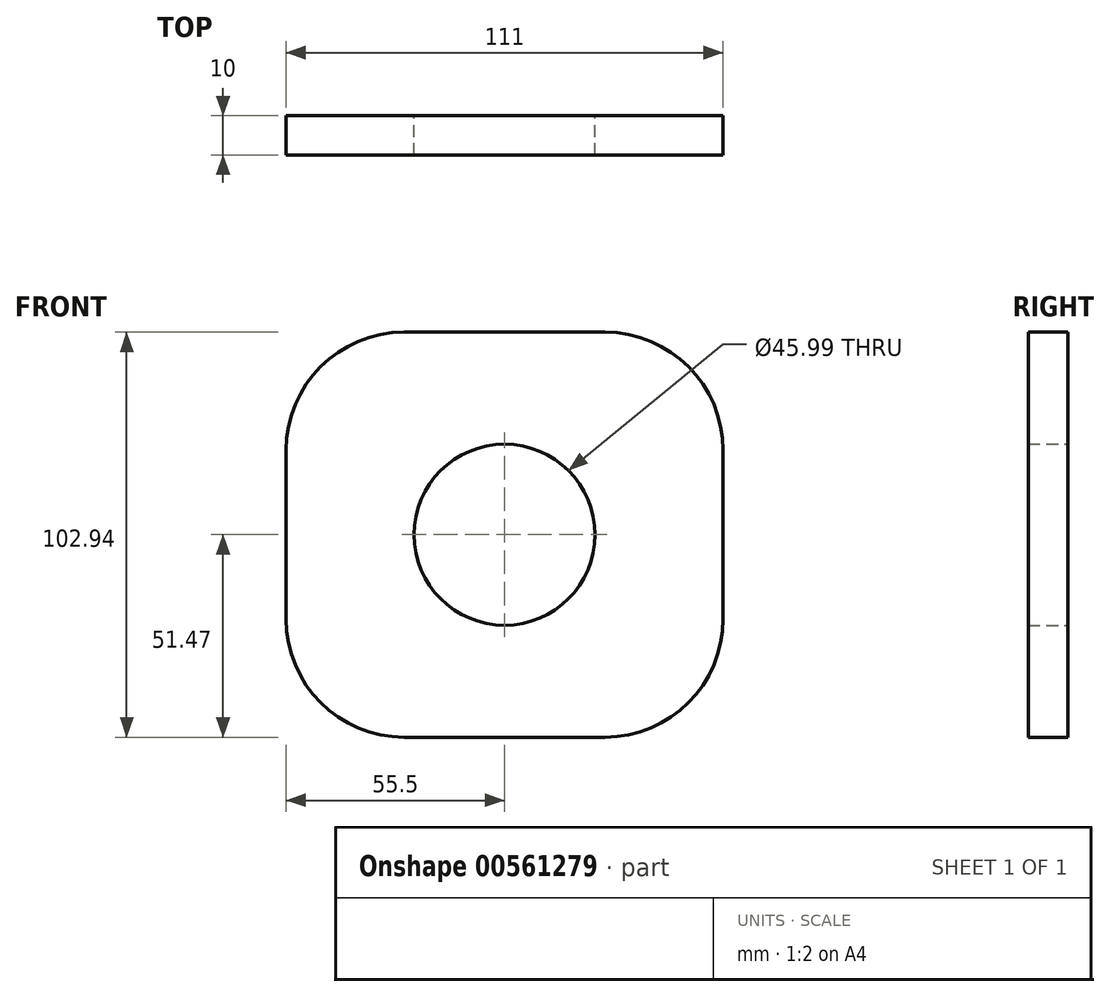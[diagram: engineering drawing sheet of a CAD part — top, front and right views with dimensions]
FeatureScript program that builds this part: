
annotation { "Feature Type Name" : "Feature", "Feature Type Description" : "" }
export const myFeature = defineFeature(function(context is Context, id is Id, definition is map)
    precondition{}
    {
        {
            var Q0;
            Q0=qCreatedBy(makeId("Front.planeOp"),FACE);
            var sketch = newSketch(context, id + "F0", { "sketchPlane" : qUnion([Q0])});
            skLineSegment(sketch, "E0.bottom", {"start": v(55.5, 51.47) * mm, "end": v(-55.5, 51.47) * mm});
            skLineSegment(sketch, "E0.top", {"start": v(55.5, -51.47) * mm, "end": v(-55.5, -51.47) * mm});
            skLineSegment(sketch, "E0.left", {"start": v(55.5, 51.47) * mm, "end": v(55.5, -51.47) * mm});
            skLineSegment(sketch, "E0.right", {"start": v(-55.5, 51.47) * mm, "end": v(-55.5, -51.47) * mm});
            skPoint(sketch, "E0.middle", {"position": v(0, 0) * mm});
            skCircle(sketch, "E1", {"center": v(0, 0) * mm, "radius": 23 * mm});
            skSolve(sketch);
        }
        {
            var Q0;
            Q0=makeQuery(id+"F0.imprint","IMPRINT",FACE,{"disambiguationData":[TD([[makeQuery(id+"F0.imprint","IMPRINT",EDGE,{"derivedFrom":sQuery(id+"F0.wireOp",EDGE,"E0.bottom")}),1.0]])]});
            extrude(context, id + "F1", {"entities" : qUnion([Q0]), "depth" : 10 * mm, "offsetDistance" : 25 * mm});
        }
        {
            var Q0;
            Q0=makeQuery(id+"F1.opExtrude","SWEPT_EDGE",EDGE,{"disambiguationData":[OSD([sQuery(id+"F0.wireOp",EDGE,"E0.bottom"),sQuery(id+"F0.wireOp",EDGE,"E0.right")])]});
            var Q1;
            Q1=makeQuery(id+"F1.opExtrude","SWEPT_EDGE",EDGE,{"disambiguationData":[OSD([sQuery(id+"F0.wireOp",EDGE,"E0.top"),sQuery(id+"F0.wireOp",EDGE,"E0.right")])]});
            var Q2;
            Q2=makeQuery(id+"F1.opExtrude","SWEPT_EDGE",EDGE,{"disambiguationData":[OSD([sQuery(id+"F0.wireOp",EDGE,"E0.top"),sQuery(id+"F0.wireOp",EDGE,"E0.left")])]});
            var Q3;
            Q3=makeQuery(id+"F1.opExtrude","SWEPT_EDGE",EDGE,{"disambiguationData":[OSD([sQuery(id+"F0.wireOp",EDGE,"E0.bottom"),sQuery(id+"F0.wireOp",EDGE,"E0.left")])]});
            fillet(context, id + "F2", {"entities" : qUnion([Q0, Q1, Q2, Q3]), "radius" : 30 * mm, "tangentPropagation" : true, "allowEdgeOverflow" : false});
        }
    });
